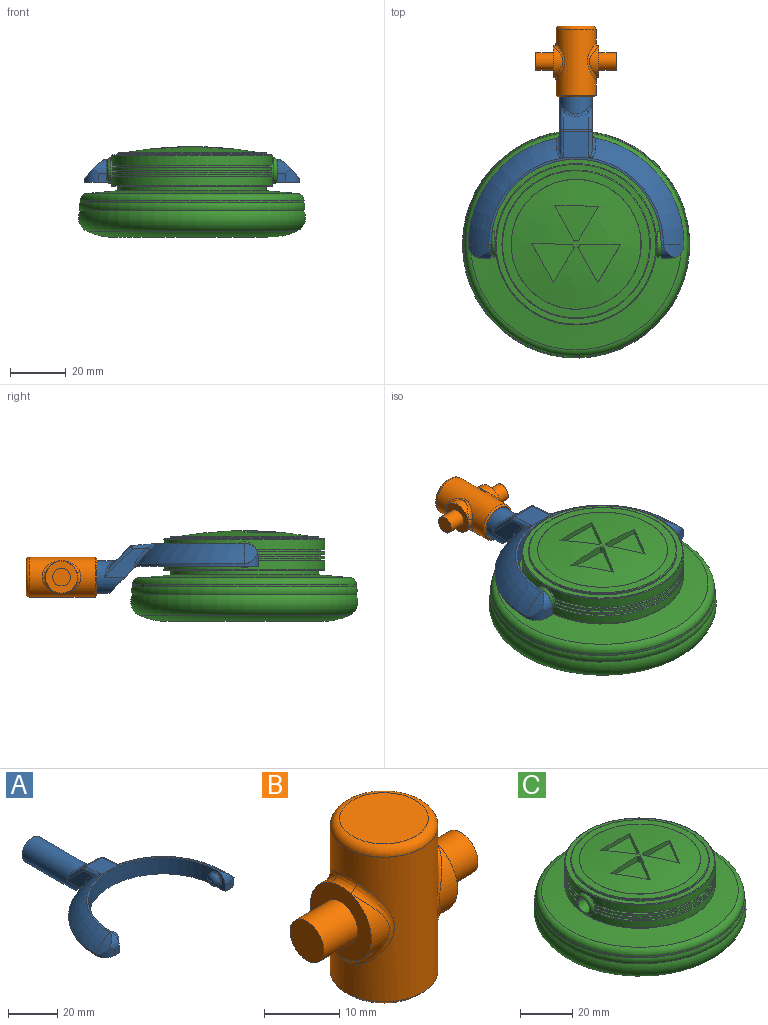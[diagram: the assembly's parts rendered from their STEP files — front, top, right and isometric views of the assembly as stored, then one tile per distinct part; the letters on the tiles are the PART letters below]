
ASSEMBLY  parts=3 mates=2
PART A: 48 faces, bbox 77.3x80.8x18.2 mm
  f0: plane 11.99x9.83mm, normal (0,-0.71,-0.71), area 141.5mm2, adj f1,f2,f9,f30,f43,f46
  f1: plane 15.39x10.49mm, normal (-1,0,0), area 63.5mm2, adj f0,f30,f32,f36,f46,f47
  f2: plane 15.39x10.49mm, normal (1,0,0), area 63.5mm2, adj f0,f30,f34,f39,f43,f44
  f3: plane 9.14x6.37mm, normal (0,0.71,0.71), area 67.6mm2, adj f35,f36,f39,f40
  f4: cylinder r=38.61mm len=37.99mm, axis (0,0,-1), area 42.6mm2, adj f6,f9,f17,f46,f47
  f5: torus R=19.3mm, axis (0,0,-1), area 507.8mm2, adj f10,f11,f12,f29,f42,f44
  f6: torus R=19.3mm, axis (0,0,-1), area 507.8mm2, adj f4,f11,f15,f28,f45,f47
  f7: cylinder r=30.48mm len=60.96mm, axis (0,0,-1), area 746.6mm2, adj f8,f9,f11,f14,f21,f24
  f8: plane 8.13x5.08mm, normal (-1,0,0), area 19.9mm2, adj f7,f9,f13,f19,f24
  f9: plane 77.22x43.73mm, normal (0,0,-1), area 956.2mm2, adj f0,f4,f7,f8,f10,f13,f14,f16
  f10: cylinder r=38.61mm len=37.99mm, axis (0,0,-1), area 42.6mm2, adj f5,f9,f20,f43,f44
  f11: plane 62.55x30.95mm, normal (0,0,1), area 75mm2, adj f5,f6,f7,f18,f19,f27
  f12: cylinder r=22.71mm len=7.33mm, axis (0,1,0), area 24.8mm2, adj f5,f19,f20
  f13: plane 3.05x3.05mm, normal (0,-1,0), area 9.3mm2, adj f8,f9,f19,f20
  f14: plane 8.13x5.08mm, normal (1,0,0), area 19.9mm2, adj f7,f9,f16,f18,f21
  f15: cylinder r=22.71mm len=7.33mm, axis (0,1,0), area 24.8mm2, adj f6,f17,f18
  f16: plane 3.05x3.05mm, normal (0,-1,0), area 9.3mm2, adj f9,f14,f17,f18
  f17: cylinder r=5.08mm len=5.08mm, axis (0,0,-1), area 21.9mm2, adj f4,f9,f15,f16,f18
  f18: cylinder r=5.08mm len=5.08mm, axis (-1,0,0), area 21.9mm2, adj f11,f14,f15,f16,f17
  f19: cylinder r=5.08mm len=5.08mm, axis (-1,0,0), area 21.9mm2, adj f8,f11,f12,f13,f20
  f20: cylinder r=5.08mm len=5.08mm, axis (0,0,-1), area 21.9mm2, adj f9,f10,f12,f13,f19
  f21: cylinder r=3.17mm len=6.35mm, axis (-1,0,0), area 12.7mm2, adj f7,f14,f23
  f22: plane 1.27x1.27mm, normal (1,0,0), area 1.3mm2, adj f23
  f23: torus R=0.64mm, axis (1,0,0), area 56.5mm2, adj f21,f22
  f24: cylinder r=3.17mm len=6.35mm, axis (1,0,0), area 12.7mm2, adj f7,f8,f26
  f25: plane 1.27x1.27mm, normal (-1,0,0), area 1.3mm2, adj f26
  f26: torus R=0.64mm, axis (-1,0,0), area 56.5mm2, adj f24,f25
  f27: plane 9.86x9.36mm, normal (0,0.09,1), area 85.6mm2, adj f11,f28,f29,f32,f34,f35,f42,f45
  f28: plane 1.04x0.17mm, normal (0,-1,0), area 0mm2, adj f6,f27,f45
  f29: plane 1.04x0.17mm, normal (0,-1,0), area 0mm2, adj f5,f27,f42
  f30: cylinder r=5.84mm len=33.01mm, axis (0,-1,0), area 1029.7mm2, adj f0,f1,f2,f31,f38,f40,f41
  f31: plane 11.68x11.68mm, normal (0,1,0), area 107.2mm2, adj f30
  f32: cylinder r=1.27mm len=9.13mm, axis (0,-1,0.09), area 14.4mm2, adj f1,f27,f33,f45
  f33: sphere r=1.27mm, area 1.5mm2, adj f32,f35,f36
  f34: cylinder r=1.27mm len=9.13mm, axis (0,1,-0.09), area 14.4mm2, adj f2,f27,f37,f42
  f35: cylinder r=1.27mm len=9.14mm, axis (-1,0,0), area 8.1mm2, adj f3,f27,f33,f37
  f36: cylinder r=1.27mm len=10.91mm, axis (0,-0.71,0.71), area 23.1mm2, adj f1,f3,f33,f38
  f37: sphere r=1.27mm, area 1.5mm2, adj f34,f35,f39
  f38: bspline ~4.55x2.75mm, area 2.3mm2, adj f30,f36,f40
  f39: cylinder r=1.27mm len=10.91mm, axis (0,0.71,-0.71), area 23.1mm2, adj f2,f3,f37,f41
  f40: bspline ~9.14x2.56mm, area 10.7mm2, adj f3,f30,f38,f41
  f41: bspline ~5.23x3.53mm, area 2.3mm2, adj f30,f39,f40
  f42: bspline ~4.62x3.14mm, area 5.2mm2, adj f5,f27,f29,f34,f44
  f43: cylinder r=1.27mm len=1.74mm, axis (0,0,-1), area 1.9mm2, adj f0,f2,f9,f10,f44
  f44: bspline ~8.6x7.86mm, area 11.9mm2, adj f2,f5,f10,f42,f43
  f45: bspline ~4.62x3.14mm, area 5.2mm2, adj f6,f27,f28,f32,f47
  f46: cylinder r=1.27mm len=1.74mm, axis (0,0,-1), area 1.9mm2, adj f0,f1,f4,f9,f47
  f47: bspline ~8.6x7.86mm, area 11.9mm2, adj f1,f4,f6,f45,f46
PART B: 25 faces, bbox 28.9x15.5x25.4 mm
  f0: cylinder r=5.71mm len=10.81mm, axis (-1,0,0), area 26.2mm2, adj f5,f15
  f1: cylinder r=5.71mm len=10.81mm, axis (-1,0,0), area 26.2mm2, adj f8,f11
  f2: cylinder r=7.14mm len=23.5mm, axis (0,0,-1), area 763.2mm2, adj f9,f10,f11,f12,f13,f14,f15,f16
  f3: plane 11.75x11.75mm, normal (0,0,1), area 108.4mm2, adj f17
  f4: plane 13.02x13.02mm, normal (0,0,-1), area 16.3mm2, adj f22,f24
  f5: plane 11.46x11.46mm, normal (1,0,0), area 70.9mm2, adj f0,f6,f13,f16,f18
  f6: cylinder r=5.71mm len=10.81mm, axis (-1,0,0), area 26.2mm2, adj f5,f14
  f7: cylinder r=5.71mm len=10.81mm, axis (-1,0,0), area 26.2mm2, adj f8,f10
  f8: plane 11.46x11.46mm, normal (-1,0,0), area 70.9mm2, adj f1,f7,f9,f12,f20
  f9: bspline ~4.64x1.73mm, area 6.5mm2, adj f2,f8,f10,f11
  f10: bspline ~13.62x4.91mm, area 20.7mm2, adj f2,f7,f9,f12
  f11: bspline ~13.6x4.87mm, area 20.7mm2, adj f1,f2,f9,f12
  f12: bspline ~4.64x1.73mm, area 6.5mm2, adj f2,f8,f10,f11
  f13: bspline ~4.64x1.73mm, area 6.5mm2, adj f2,f5,f14,f15
  f14: bspline ~13.62x4.91mm, area 20.7mm2, adj f2,f6,f13,f16
  f15: bspline ~13.6x4.87mm, area 20.7mm2, adj f0,f2,f13,f16
  f16: bspline ~4.64x1.73mm, area 6.5mm2, adj f2,f5,f14,f15
  f17: torus R=5.87mm, axis (0,0,1), area 83.8mm2, adj f2,f3
  f18: cylinder r=3.17mm len=6.35mm, axis (-1,0,0), area 126.7mm2, adj f5,f19
  f19: plane 6.35x6.35mm, normal (1,0,0), area 31.7mm2, adj f18
  f20: cylinder r=3.17mm len=6.35mm, axis (1,0,0), area 126.7mm2, adj f8,f21
  f21: plane 6.35x6.35mm, normal (-1,0,0), area 31.7mm2, adj f20
  f22: cylinder r=6.1mm len=22.86mm, axis (0,0,-1), area 875.6mm2, adj f4,f23
  f23: plane 12.19x12.19mm, normal (0,0,-1), area 116.7mm2, adj f22
  f24: cone r=7.14mm half-angle=45deg, axis (0,0,1), area 38.5mm2, adj f2,f4
PART C: 64 faces, bbox 96.3x96.3x32.5 mm
  f0: cylinder r=28.87mm len=57.73mm, axis (0,0,-1), area 562.1mm2, adj f3,f4,f54,f55,f60
  f1: cylinder r=27.6mm len=54.59mm, axis (0,0,1), area 49.7mm2, adj f3,f6,f54,f55
  f2: cylinder r=27.6mm len=54.59mm, axis (0,0,1), area 49.7mm2, adj f4,f5,f54,f55
  f3: plane 57.16x24.81mm, normal (0,0,1), area 102.3mm2, adj f0,f1,f54,f55
  f4: plane 57.16x24.81mm, normal (0,0,1), area 102.3mm2, adj f0,f2,f54,f55
  f5: plane 57.08x24.54mm, normal (0,0,-1), area 101.6mm2, adj f2,f7,f54,f55
  f6: plane 57.08x24.54mm, normal (0,0,-1), area 101.6mm2, adj f1,f8,f54,f55
  f7: cylinder r=28.87mm len=57.08mm, axis (0,0,-1), area 77.9mm2, adj f5,f11,f54,f55
  f8: cylinder r=28.87mm len=57.08mm, axis (0,0,-1), area 77.9mm2, adj f6,f12,f54,f55
  f9: cylinder r=27.6mm len=54.44mm, axis (0,0,1), area 49.2mm2, adj f12,f13,f54,f55
  f10: cylinder r=27.6mm len=54.44mm, axis (0,0,1), area 49.2mm2, adj f11,f14,f54,f55
  f11: plane 57.02x24.33mm, normal (0,0,1), area 101.1mm2, adj f7,f10,f54,f55
  f12: plane 57.02x24.33mm, normal (0,0,1), area 101.1mm2, adj f8,f9,f54,f55
  f13: plane 57.01x24.3mm, normal (0,0,-1), area 101mm2, adj f9,f16,f54,f55
  f14: plane 57.01x24.3mm, normal (0,0,-1), area 101mm2, adj f10,f15,f54,f55
  f15: cylinder r=28.87mm len=57.05mm, axis (0,0,-1), area 77.8mm2, adj f14,f20,f54,f55
  f16: cylinder r=28.87mm len=57.05mm, axis (0,0,-1), area 77.8mm2, adj f13,f19,f54,f55
  f17: cylinder r=27.6mm len=54.54mm, axis (0,0,1), area 49.5mm2, adj f19,f22,f54,f55
  f18: cylinder r=27.6mm len=54.54mm, axis (0,0,1), area 49.5mm2, adj f20,f21,f54,f55
  f19: plane 57.05x24.42mm, normal (0,0,1), area 101.3mm2, adj f16,f17,f54,f55
  f20: plane 57.05x24.42mm, normal (0,0,1), area 101.3mm2, adj f15,f18,f54,f55
  f21: plane 57.11x24.62mm, normal (0,0,-1), area 101.8mm2, adj f18,f23,f54,f55
  f22: plane 57.11x24.62mm, normal (0,0,-1), area 101.8mm2, adj f17,f23,f54,f55
  f23: cylinder r=28.87mm len=57.73mm, axis (0,0,-1), area 629.3mm2, adj f21,f22,f54,f55,f61
  f24: sphere r=135.39mm, area 1385.3mm2, adj f38,f39,f40,f41,f43,f44,f45,f46
  f25: plane 39.35x39.35mm, normal (0,0,-1), area 1216.2mm2, adj f26
  f26: torus R=20.13mm, axis (0,0,-1), area 1430.4mm2, adj f25,f27
  f27: torus R=27.75mm, axis (0,0,-1), area 3543.7mm2, adj f26,f28
  f28: torus R=35.37mm, axis (0,0,-1), area 2180.8mm2, adj f27,f29
  f29: torus R=37.36mm, axis (0,0,-1), area 734.8mm2, adj f28,f30
  f30: cylinder r=40.07mm len=80.14mm, axis (0,0,-1), area 213.4mm2, adj f29,f34
  f31: cone r=26.58mm half-angle=85deg, axis (0,0,-1), area 2265.9mm2, adj f32,f34
  f32: cylinder r=26.58mm len=53.16mm, axis (0,0,-1), area 265.1mm2, adj f31,f33
  f33: plane 57.23x57.23mm, normal (0,0,-1), area 352.3mm2, adj f32,f60
  f34: torus R=37.53mm, axis (0,0,1), area 928.9mm2, adj f30,f31
  f35: cone r=26.58mm half-angle=87deg, axis (0,0,-1), area 477.5mm2, adj f62,f63
  f36: cylinder r=26.58mm len=53.16mm, axis (0,0,-1), area 92.3mm2, adj f37,f62
  f37: plane 57.23x57.23mm, normal (0,0,1), area 352.3mm2, adj f36,f61
  f38: cylinder r=1.27mm len=2.53mm, axis (0,0,1), area 3.4mm2, adj f24,f39,f41,f42
  f39: plane 14.6x2.53mm, normal (-0.01,-1,0), area 32.2mm2, adj f24,f38,f40,f42
  f40: plane 13.85x7.76mm, normal (0.87,0.49,0), area 28mm2, adj f24,f39,f41,f42
  f41: plane 12.55x7.46mm, normal (-0.86,0.51,0), area 32.2mm2, adj f24,f38,f40,f42
  f42: plane 15.22x13.85mm, normal (0,0,1), area 108.3mm2, adj f38,f39,f40,f41
  f43: cylinder r=1.27mm len=2.53mm, axis (0,0,1), area 3.4mm2, adj f24,f44,f46,f47
  f44: plane 12.74x7.14mm, normal (0.87,0.49,0), area 32.2mm2, adj f24,f43,f45,f47
  f45: plane 13.65x8.11mm, normal (-0.86,0.51,0), area 28mm2, adj f24,f44,f46,f47
  f46: plane 14.6x2.53mm, normal (-0.01,-1,0), area 32.2mm2, adj f24,f43,f45,f47
  f47: plane 15.25x13.83mm, normal (0,0,1), area 108.3mm2, adj f43,f44,f45,f46
  f48: cylinder r=1.27mm len=2.53mm, axis (0,0,1), area 3.4mm2, adj f24,f49,f51,f52
  f49: plane 12.55x7.46mm, normal (-0.86,0.51,0), area 32.2mm2, adj f24,f48,f50,f52
  f50: plane 15.87x1.84mm, normal (-0.01,-1,0), area 28mm2, adj f24,f49,f51,f52
  f51: plane 12.74x7.14mm, normal (0.87,0.49,0), area 32.2mm2, adj f24,f48,f50,f52
  f52: plane 15.87x12.76mm, normal (0,0,1), area 108.3mm2, adj f48,f49,f50,f51
  f53: plane 6.6x6.6mm, normal (1,0,0), area 2.6mm2, adj f58,f59
  f54: cylinder r=4.57mm len=9.14mm, axis (-1,0,0), area 20.2mm2, adj f0,f1,f2,f3,f4,f5,f6,f7
  f55: cylinder r=4.57mm len=9.14mm, axis (-1,0,0), area 20.2mm2, adj f0,f1,f2,f3,f4,f5,f6,f7
  f56: plane 6.6x6.6mm, normal (-1,0,0), area 2.6mm2, adj f57,f59
  f57: torus R=3.3mm, axis (1,0,0), area 51.5mm2, adj f55,f56
  f58: torus R=3.3mm, axis (1,0,0), area 51.5mm2, adj f53,f54
  f59: cylinder r=3.17mm len=60.96mm, axis (1,0,0), area 1216.1mm2, adj f53,f56
  f60: torus R=28.61mm, axis (0,0,1), area 72.1mm2, adj f0,f33
  f61: torus R=28.61mm, axis (0,0,-1), area 72.1mm2, adj f23,f37
  f62: torus R=26.33mm, axis (0,0,1), area 64.2mm2, adj f35,f36
  f63: torus R=23.29mm, axis (0,0,1), area 4.5mm2, adj f24,f35
PLACE A t=(32.34,27.52,20.85)mm
PLACE B rot(axis=(-1,0,0),90deg) t=(32.34,80.3,16.88)mm
PLACE C t=(32.34,27.52,33.52)mm
MATE revolute A.f24 <-> C.f54  axis (-1,0,0) through (62.82,27.52,24.92)mm
MATE revolute B.f2 <-> A.f30  axis (0,-1,0) through (32.34,103.16,16.88)mm
